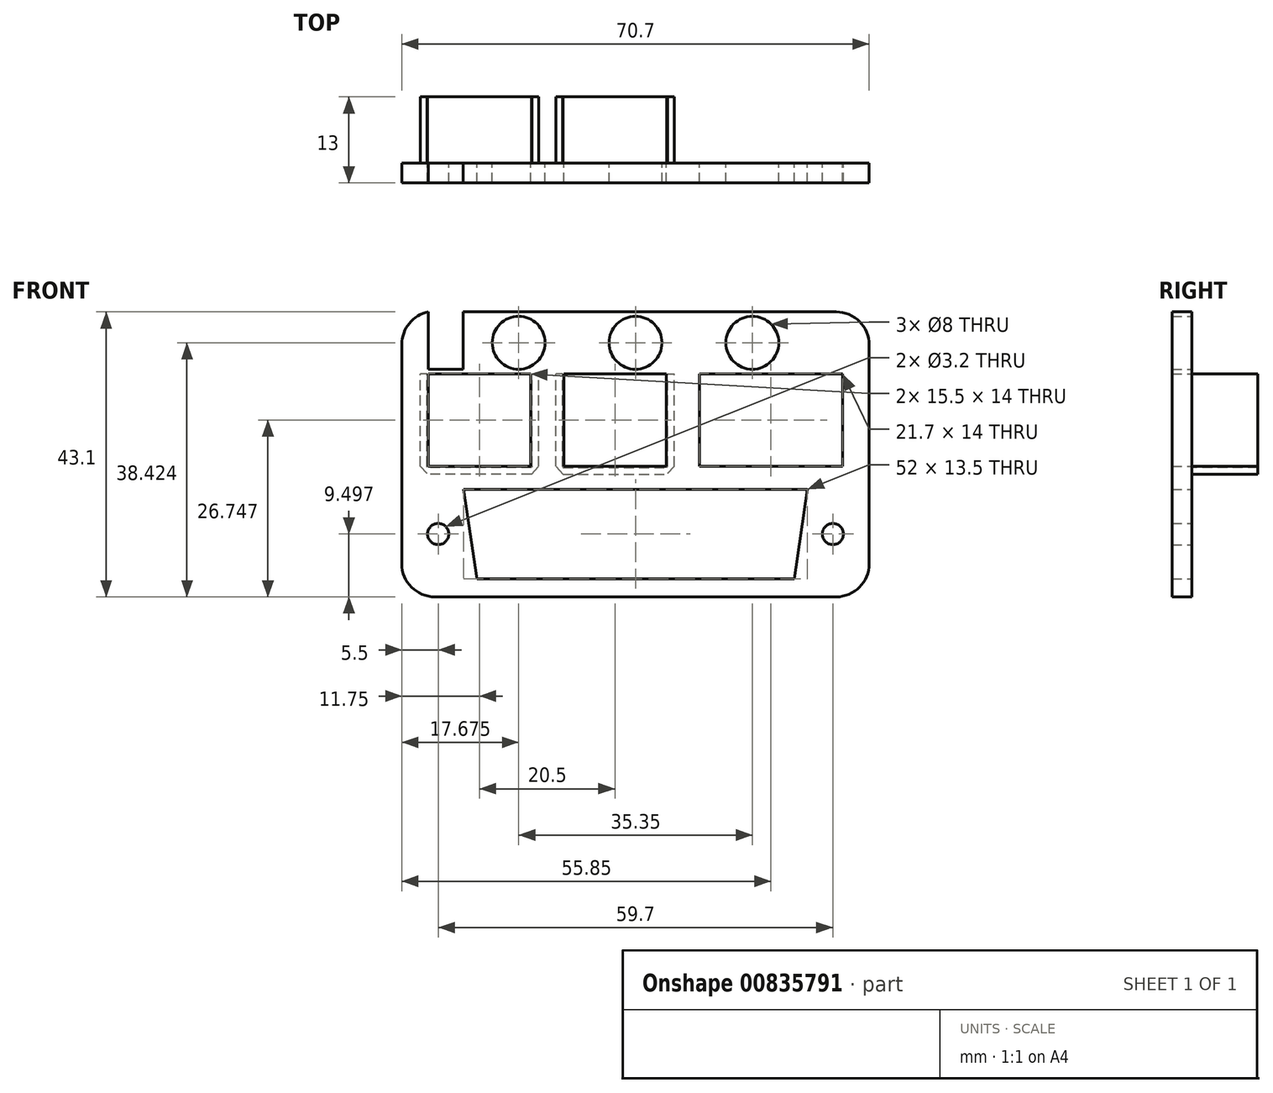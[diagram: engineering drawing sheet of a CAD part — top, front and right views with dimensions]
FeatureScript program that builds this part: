
annotation { "Feature Type Name" : "Feature", "Feature Type Description" : "" }
export const myFeature = defineFeature(function(context is Context, id is Id, definition is map)
    precondition{}
    {
        {
            var Q0;
            Q0=qCreatedBy(makeId("Front.planeOp"),FACE);
            var sketch = newSketch(context, id + "F0", { "sketchPlane" : qUnion([Q0])});
            skLineSegment(sketch, "E0.bottom", {"start": v(-35.35, -21.55) * mm, "end": v(35.35, -21.55) * mm});
            skLineSegment(sketch, "E0.top", {"start": v(-35.35, 21.55) * mm, "end": v(35.35, 21.55) * mm});
            skLineSegment(sketch, "E0.left", {"start": v(-35.35, -21.55) * mm, "end": v(-35.35, 21.55) * mm});
            skLineSegment(sketch, "E0.right", {"start": v(35.35, -21.55) * mm, "end": v(35.35, 21.55) * mm});
            skPoint(sketch, "E0.middle", {"position": v(0, 0) * mm});
            skSolve(sketch);
        }
        {
            var Q0;
            Q0=makeQuery(id+"F0.imprint","IMPRINT",FACE,{"disambiguationData":[TD([[makeQuery(id+"F0.imprint","IMPRINT",EDGE,{"derivedFrom":sQuery(id+"F0.wireOp",EDGE,"E0.bottom")}),1.0]])]});
            var sketch = newSketch(context, id + "F1", { "sketchPlane" : qUnion([Q0])});
            skLineSegment(sketch, "E1", {"start": v(0, -18.8) * mm, "end": v(24, -18.8) * mm});
            skLineSegment(sketch, "E2", {"start": v(0, -18.8) * mm, "end": v(0, -5.3) * mm});
            skLineSegment(sketch, "E3", {"start": v(0, -5.3) * mm, "end": v(26, -5.3) * mm});
            skLineSegment(sketch, "E4", {"start": v(26, -5.3) * mm, "end": v(24, -18.8) * mm});
            skLineSegment(sketch, "E5.MirrorCS", {"start": v(0, -5.3) * mm, "end": v(-26, -5.3) * mm});
            skLineSegment(sketch, "E6.MirrorCS", {"start": v(-26, -5.3) * mm, "end": v(-24, -18.8) * mm});
            skLineSegment(sketch, "E7.MirrorCS", {"start": v(0, -18.8) * mm, "end": v(-24, -18.8) * mm});
            skLineSegment(sketch, "E8", {"start": v(0, -12.05) * mm, "end": v(-29.85, -12.05) * mm});
            skCircle(sketch, "E9", {"center": v(-29.85, -12.05) * mm, "radius": 1.6 * mm});
            skCircle(sketch, "E10.MirrorC", {"center": v(29.85, -12.05) * mm, "radius": 1.6 * mm});
            skSolve(sketch);
        }
        {
            var Q0;
            Q0=makeQuery(id+"F0.imprint","IMPRINT",FACE,{"disambiguationData":[TD([[makeQuery(id+"F0.imprint","IMPRINT",EDGE,{"derivedFrom":sQuery(id+"F0.wireOp",EDGE,"E0.bottom")}),1.0]])]});
            var sketch = newSketch(context, id + "F2", { "sketchPlane" : qUnion([Q0])});
            skLineSegment(sketch, "E11", {"start": v(-15.58, -5.3) * mm, "end": v(-15.58, -1.8) * mm});
            skLineSegment(sketch, "E12", {"start": v(-35.35, -1.8) * mm, "end": v(35.35, -1.8) * mm});
            skLineSegment(sketch, "E13", {"start": v(-35.35, -1.8) * mm, "end": v(-31.35, -1.8) * mm});
            skLineSegment(sketch, "E14.bottom", {"start": v(-31.35, -1.8) * mm, "end": v(-15.85, -1.8) * mm});
            skLineSegment(sketch, "E14.top", {"start": v(-31.35, 12.2) * mm, "end": v(-15.85, 12.2) * mm});
            skLineSegment(sketch, "E14.left", {"start": v(-31.35, -1.8) * mm, "end": v(-31.35, 12.2) * mm});
            skLineSegment(sketch, "E14.right", {"start": v(-15.85, -1.8) * mm, "end": v(-15.85, 12.2) * mm});
            skLineSegment(sketch, "E15", {"start": v(-15.85, -1.8) * mm, "end": v(-10.85, -1.8) * mm});
            skLineSegment(sketch, "E16.bottom", {"start": v(-10.85, -1.8) * mm, "end": v(4.65, -1.8) * mm});
            skLineSegment(sketch, "E16.top", {"start": v(-10.85, 12.2) * mm, "end": v(4.65, 12.2) * mm});
            skLineSegment(sketch, "E16.left", {"start": v(-10.85, -1.8) * mm, "end": v(-10.85, 12.2) * mm});
            skLineSegment(sketch, "E16.right", {"start": v(4.65, -1.8) * mm, "end": v(4.65, 12.2) * mm});
            skLineSegment(sketch, "E17", {"start": v(4.65, -1.8) * mm, "end": v(9.65, -1.8) * mm});
            skLineSegment(sketch, "E18", {"start": v(35.35, -1.8) * mm, "end": v(31.35, -1.8) * mm});
            skLineSegment(sketch, "E19.bottom", {"start": v(9.65, -1.8) * mm, "end": v(31.35, -1.8) * mm});
            skLineSegment(sketch, "E19.top", {"start": v(9.65, 12.2) * mm, "end": v(31.35, 12.2) * mm});
            skLineSegment(sketch, "E19.left", {"start": v(9.65, -1.8) * mm, "end": v(9.65, 12.2) * mm});
            skLineSegment(sketch, "E19.right", {"start": v(31.35, -1.8) * mm, "end": v(31.35, 12.2) * mm});
            skLineSegment(sketch, "E20", {"start": v(0, 21.55) * mm, "end": v(0, 12.2) * mm});
            skLineSegment(sketch, "E21", {"start": v(0, 16.87) * mm, "end": v(35.35, 16.87) * mm});
            skLineSegment(sketch, "E22.MirrorCS", {"start": v(0, 16.87) * mm, "end": v(-35.35, 16.87) * mm});
            skCircle(sketch, "E23", {"center": v(0, 16.87) * mm, "radius": 4 * mm});
            skCircle(sketch, "E24", {"center": v(-17.67, 16.87) * mm, "radius": 4 * mm});
            skCircle(sketch, "E25", {"center": v(17.67, 16.87) * mm, "radius": 4 * mm});
            skLineSegment(sketch, "E26", {"start": v(-35.35, 16.87) * mm, "end": v(-31.35, 16.87) * mm});
            skLineSegment(sketch, "E27.bottom", {"start": v(-31.35, 16.87) * mm, "end": v(-26.05, 16.87) * mm});
            skLineSegment(sketch, "E27.top", {"start": v(-31.35, 21.55) * mm, "end": v(-26.05, 21.55) * mm});
            skLineSegment(sketch, "E27.left", {"start": v(-31.35, 16.87) * mm, "end": v(-31.35, 21.55) * mm});
            skLineSegment(sketch, "E27.right", {"start": v(-26.05, 16.87) * mm, "end": v(-26.05, 21.55) * mm});
            skLineSegment(sketch, "E28.top", {"start": v(-31.35, 12.87) * mm, "end": v(-26.05, 12.87) * mm});
            skLineSegment(sketch, "E28.left", {"start": v(-31.35, 16.87) * mm, "end": v(-31.35, 12.87) * mm});
            skLineSegment(sketch, "E28.right", {"start": v(-26.05, 16.87) * mm, "end": v(-26.05, 12.87) * mm});
            skSolve(sketch);
        }
        {
            var Q0;
            Q0=qSketchRegion(id+"F0",true);
            extrude(context, id + "F3", {"entities" : qUnion([Q0]), "depth" : 3 * mm, "offsetDistance" : 25 * mm});
        }
        {
            var Q0;
            Q0=qSketchRegion(id+"F1",true);
            extrude(context, id + "F4", {"entities" : qUnion([Q0]), "operationType" : NewBodyOperationType.REMOVE, "oppositeDirection" : true, "depth" : -3 * mm, "offsetDistance" : 25 * mm});
        }
        {
            var Q0;
            Q0=qSketchRegion(id+"F2",true);
            extrude(context, id + "F5", {"entities" : qUnion([Q0]), "operationType" : NewBodyOperationType.REMOVE, "oppositeDirection" : true, "depth" : -3 * mm, "offsetDistance" : 25 * mm});
        }
        {
            var Q0;
            Q0=makeQuery(id+"F3.opExtrude","SWEPT_EDGE",EDGE,{"disambiguationData":[OSD([sQuery(id+"F0.wireOp",EDGE,"E0.top"),sQuery(id+"F0.wireOp",EDGE,"E0.left")])]});
            var Q1;
            Q1=makeQuery(id+"F3.opExtrude","SWEPT_EDGE",EDGE,{"disambiguationData":[OSD([sQuery(id+"F0.wireOp",EDGE,"E0.top"),sQuery(id+"F0.wireOp",EDGE,"E0.right")])]});
            var Q2;
            Q2=makeQuery(id+"F3.opExtrude","SWEPT_EDGE",EDGE,{"disambiguationData":[OSD([sQuery(id+"F0.wireOp",EDGE,"E0.bottom"),sQuery(id+"F0.wireOp",EDGE,"E0.right")])]});
            var Q3;
            Q3=makeQuery(id+"F3.opExtrude","SWEPT_EDGE",EDGE,{"disambiguationData":[OSD([sQuery(id+"F0.wireOp",EDGE,"E0.bottom"),sQuery(id+"F0.wireOp",EDGE,"E0.left")])]});
            fillet(context, id + "F6", {"entities" : qUnion([Q0, Q1, Q2, Q3]), "radius" : 5 * mm, "tangentPropagation" : true, "allowEdgeOverflow" : false});
        }
        {
            var Q0;
            Q0=makeQuery(id+"F3.opExtrude","CAP_FACE",FACE,{"disambiguationData":[OSD([sQuery(id+"F0.wireOp",EDGE,"E0.bottom"),sQuery(id+"F0.wireOp",EDGE,"E0.top"),sQuery(id+"F0.wireOp",EDGE,"E0.left"),sQuery(id+"F0.wireOp",EDGE,"E0.right")])],"isStart":true});
            var sketch = newSketch(context, id + "F7", { "sketchPlane" : qUnion([Q0])});
            skLineSegment(sketch, "E29.bottom", {"start": v(15.75, -3) * mm, "end": v(31.45, -3) * mm});
            skLineSegment(sketch, "E29.top", {"start": v(15.75, -2) * mm, "end": v(31.45, -2) * mm});
            skLineSegment(sketch, "E29.left", {"start": v(15.75, -3) * mm, "end": v(15.75, -2) * mm});
            skLineSegment(sketch, "E29.right", {"start": v(31.45, -3) * mm, "end": v(31.45, -2) * mm});
            skLineSegment(sketch, "E30", {"start": v(23.6, -2) * mm, "end": v(23.6, -1.8) * mm});
            skLineSegment(sketch, "E31", {"start": v(10.85, 5.2) * mm, "end": v(15.85, 5.2) * mm});
            skLineSegment(sketch, "E32", {"start": v(13.35, 5.2) * mm, "end": v(13.35, -5.3) * mm});
            skLineSegment(sketch, "E33.MirrorCS", {"start": v(10.95, -3) * mm, "end": v(10.95, -2) * mm});
            skLineSegment(sketch, "E34.MirrorCS", {"start": v(10.95, -3) * mm, "end": v(-4.75, -3) * mm});
            skLineSegment(sketch, "E35.MirrorCS", {"start": v(10.95, -2) * mm, "end": v(-4.75, -2) * mm});
            skLineSegment(sketch, "E36.MirrorCS", {"start": v(-4.75, -3) * mm, "end": v(-4.75, -2) * mm});
            skLineSegment(sketch, "E37", {"start": v(15.85, 5.2) * mm, "end": v(15.65, 5.2) * mm});
            skLineSegment(sketch, "E38.bottom", {"start": v(15.65, -1.8) * mm, "end": v(14.65, -1.8) * mm});
            skLineSegment(sketch, "E38.top", {"start": v(15.65, 12.2) * mm, "end": v(14.65, 12.2) * mm});
            skLineSegment(sketch, "E38.left", {"start": v(15.65, -1.8) * mm, "end": v(15.65, 12.2) * mm});
            skLineSegment(sketch, "E38.right", {"start": v(14.65, -1.8) * mm, "end": v(14.65, 12.2) * mm});
            skLineSegment(sketch, "E39.MirrorCS", {"start": v(31.55, -1.8) * mm, "end": v(31.55, 12.2) * mm});
            skLineSegment(sketch, "E40.MirrorCS", {"start": v(32.55, -1.8) * mm, "end": v(32.55, 12.2) * mm});
            skLineSegment(sketch, "E41.MirrorCS", {"start": v(31.55, 12.2) * mm, "end": v(32.55, 12.2) * mm});
            skLineSegment(sketch, "E42.MirrorCS", {"start": v(31.55, -1.8) * mm, "end": v(32.55, -1.8) * mm});
            skLineSegment(sketch, "E43", {"start": v(31.45, -2) * mm, "end": v(31.55, -1.8) * mm});
            skLineSegment(sketch, "E44", {"start": v(32.55, -1.8) * mm, "end": v(31.45, -3) * mm});
            skLineSegment(sketch, "E45", {"start": v(15.65, -1.8) * mm, "end": v(15.75, -2) * mm});
            skLineSegment(sketch, "E46", {"start": v(15.75, -3) * mm, "end": v(14.65, -1.8) * mm});
            skLineSegment(sketch, "E47.MirrorCS", {"start": v(10.95, -3) * mm, "end": v(12.05, -1.8) * mm});
            skLineSegment(sketch, "E48.MirrorCS", {"start": v(12.05, -1.8) * mm, "end": v(12.05, 12.2) * mm});
            skLineSegment(sketch, "E49.MirrorCS", {"start": v(11.05, -1.8) * mm, "end": v(11.05, 12.2) * mm});
            skLineSegment(sketch, "E50.MirrorCS", {"start": v(11.05, -1.8) * mm, "end": v(12.05, -1.8) * mm});
            skLineSegment(sketch, "E51.MirrorCS", {"start": v(11.05, 12.2) * mm, "end": v(12.05, 12.2) * mm});
            skLineSegment(sketch, "E52.MirrorCS", {"start": v(-4.75, -2) * mm, "end": v(-4.85, -1.8) * mm});
            skLineSegment(sketch, "E53.MirrorCS", {"start": v(-4.85, -1.8) * mm, "end": v(-5.85, -1.8) * mm});
            skLineSegment(sketch, "E54.MirrorCS", {"start": v(-5.85, -1.8) * mm, "end": v(-4.75, -3) * mm});
            skLineSegment(sketch, "E55.MirrorCS", {"start": v(-4.85, -1.8) * mm, "end": v(-4.85, 12.2) * mm});
            skLineSegment(sketch, "E56.MirrorCS", {"start": v(-5.85, -1.8) * mm, "end": v(-5.85, 12.2) * mm});
            skLineSegment(sketch, "E57.MirrorCS", {"start": v(-4.85, 12.2) * mm, "end": v(-5.85, 12.2) * mm});
            skLineSegment(sketch, "E58.MirrorCS", {"start": v(11.05, -1.8) * mm, "end": v(10.95, -2) * mm});
            skSolve(sketch);
        }
        {
            var Q0;
            Q0=makeQuery(id+"F7.imprint","IMPRINT",FACE,{"disambiguationData":[TD([[makeQuery(id+"F7.imprint","IMPRINT",EDGE,{"derivedFrom":sQuery(id+"F7.wireOp",EDGE,"E29.bottom")}),1.0]])]});
            var Q1;
            Q1=makeQuery(id+"F7.imprint","IMPRINT",FACE,{"disambiguationData":[TD([[makeQuery(id+"F7.imprint","IMPRINT",EDGE,{"derivedFrom":sQuery(id+"F7.wireOp",EDGE,"E29.right")}),-1.0]])]});
            var Q2;
            Q2=makeQuery(id+"F7.imprint","IMPRINT",FACE,{"disambiguationData":[TD([[makeQuery(id+"F7.imprint","IMPRINT",EDGE,{"derivedFrom":sQuery(id+"F7.wireOp",EDGE,"E39.MirrorCS")}),-1.0]])]});
            var Q3;
            Q3=makeQuery(id+"F7.imprint","IMPRINT",FACE,{"disambiguationData":[TD([[makeQuery(id+"F7.imprint","IMPRINT",EDGE,{"derivedFrom":sQuery(id+"F7.wireOp",EDGE,"E29.left")}),1.0]])]});
            var Q4;
            {var subQ5=sQuery(id+"F7.wireOp",EDGE,"E38.bottom");Q4=makeQuery(id+"F7.imprint","IMPRINT",FACE,{"disambiguationData":[TD([[makeQuery(id+"F7.imprint","IMPRINT",EDGE,{"derivedFrom":subQ5}),-1.0]])]});}
            var Q5;
            {var subQ5=sQuery(id+"F7.wireOp",EDGE,"E38.top");Q5=makeQuery(id+"F7.imprint","IMPRINT",FACE,{"disambiguationData":[TD([[makeQuery(id+"F7.imprint","IMPRINT",EDGE,{"derivedFrom":subQ5}),1.0]])]});}
            var Q6;
            Q6=makeQuery(id+"F7.imprint","IMPRINT",FACE,{"disambiguationData":[TD([[makeQuery(id+"F7.imprint","IMPRINT",EDGE,{"derivedFrom":sQuery(id+"F7.wireOp",EDGE,"E33.MirrorCS")}),1.0]])]});
            var Q7;
            Q7=makeQuery(id+"F7.imprint","IMPRINT",FACE,{"disambiguationData":[TD([[makeQuery(id+"F7.imprint","IMPRINT",EDGE,{"derivedFrom":sQuery(id+"F7.wireOp",EDGE,"E36.MirrorCS")}),1.0]])]});
            var Q8;
            Q8=makeQuery(id+"F7.imprint","IMPRINT",FACE,{"disambiguationData":[TD([[makeQuery(id+"F7.imprint","IMPRINT",EDGE,{"derivedFrom":sQuery(id+"F7.wireOp",EDGE,"E53.MirrorCS")}),-1.0]])]});
            var Q9;
            {var subQ5=sQuery(id+"F7.wireOp",EDGE,"E50.MirrorCS");Q9=makeQuery(id+"F7.imprint","IMPRINT",FACE,{"disambiguationData":[TD([[makeQuery(id+"F7.imprint","IMPRINT",EDGE,{"derivedFrom":subQ5}),1.0]])]});}
            var Q10;
            {var subQ5=sQuery(id+"F7.wireOp",EDGE,"E51.MirrorCS");Q10=makeQuery(id+"F7.imprint","IMPRINT",FACE,{"disambiguationData":[TD([[makeQuery(id+"F7.imprint","IMPRINT",EDGE,{"derivedFrom":subQ5}),-1.0]])]});}
            var Q11;
            Q11=makeQuery(id+"F7.imprint","IMPRINT",FACE,{"disambiguationData":[TD([[makeQuery(id+"F7.imprint","IMPRINT",EDGE,{"derivedFrom":sQuery(id+"F7.wireOp",EDGE,"E33.MirrorCS")}),-1.0]])]});
            extrude(context, id + "F8", {"entities" : qUnion([Q0, Q1, Q2, Q3, Q4, Q5, Q6, Q7, Q8, Q9, Q10, Q11]), "operationType" : NewBodyOperationType.ADD, "depth" : 10 * mm, "offsetDistance" : 25 * mm});
        }
    });
